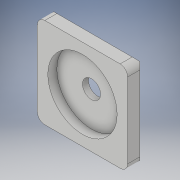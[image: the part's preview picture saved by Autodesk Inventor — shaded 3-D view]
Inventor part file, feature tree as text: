
AUTODESK INVENTOR PART (.ipt)
format: ipt  version: 2017 SP1 (Build 210196100, 196)  size: 128,000 bytes
history: native  units: in
note: dims shown in document units (in); Inventor stores cm internally (conversion verified against a paired STEP export)
features: sketch x2, extrude x1, hole x1, chamfer x1, fillet x1
ambient origin geometry x8: Origin, YZ Plane, XZ Plane, XY Plane, X Axis, Y Axis, Z Axis, Center Point
bodies: Solid1 (feature_tree)
feature tree (6):
  extrude  "Extrusion1"  Depth=1.5in
  hole  "Hole1"  [1 undecoded]
  chamfer  "Chamfer1"  Distance=0.125in
  fillet  "Fillet1"  [1 undecoded]
  sketch  "Sketch1"  dims[d0=1.5in d1=1.5in]
  sketch  "Sketch2"  dims[d2=0.25in d3=0.0in d4=0.3in d5=0.75in d6=1.15in d7=0.15in d8=0.5635in d9=1.0in d10=0.8108in d11=0.05in d12=0.125in d13=45.0deg d14=0.125in]
note: 2 required parameter values undecoded (feature->parameter linkage not recoverable at this tier; creation-order binding heuristic only, values carry confidence <= 0.55)
